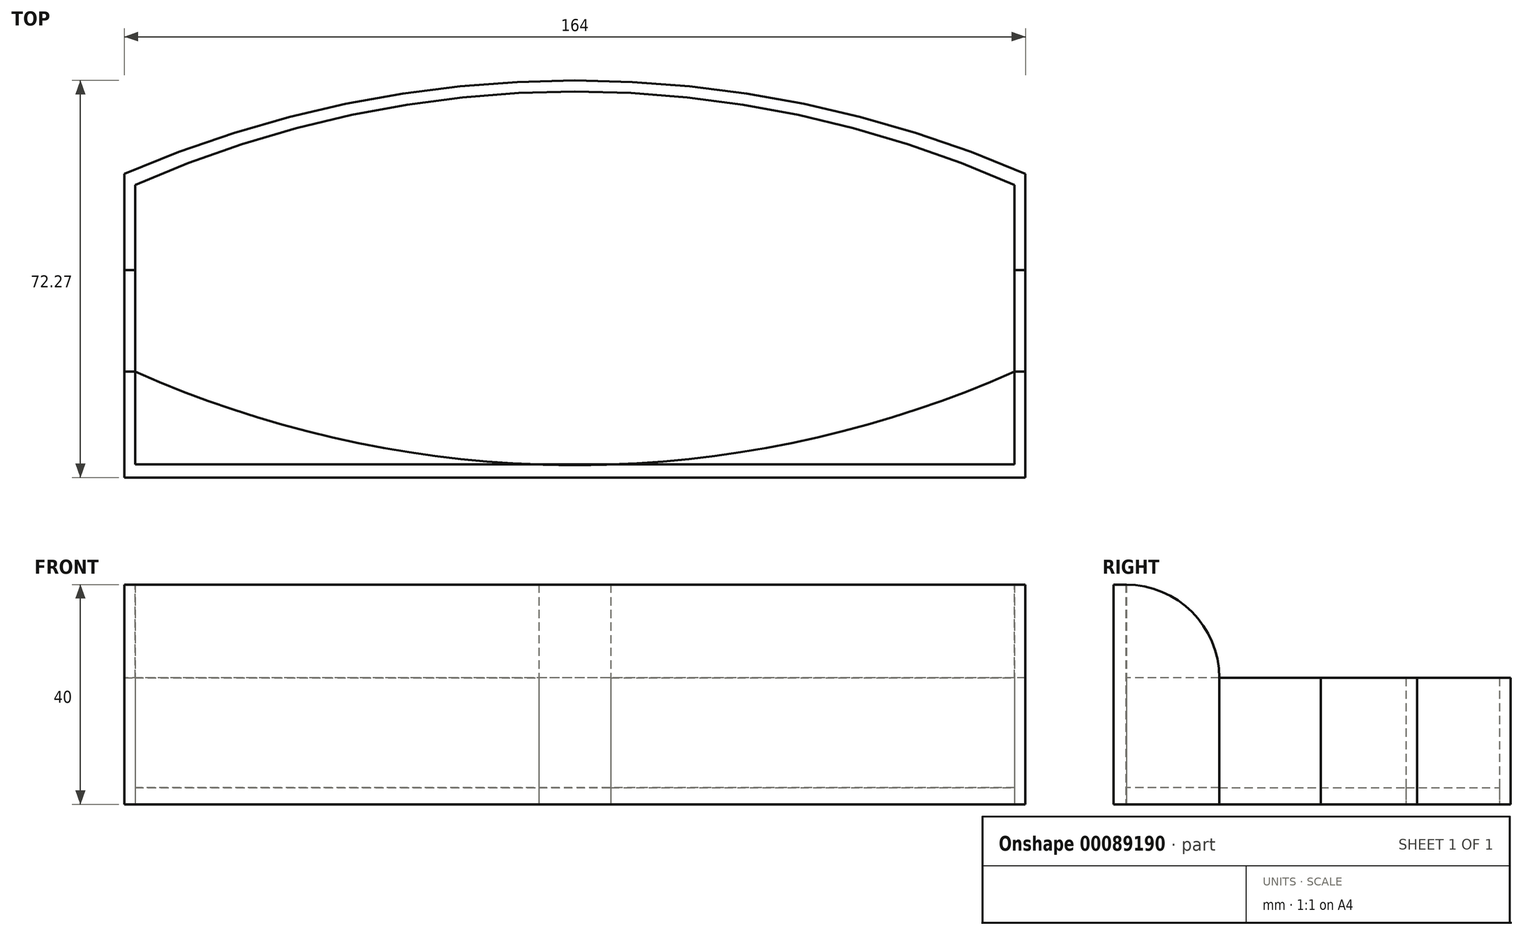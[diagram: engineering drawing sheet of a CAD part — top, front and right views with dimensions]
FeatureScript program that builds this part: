
annotation { "Feature Type Name" : "Feature", "Feature Type Description" : "" }
export const myFeature = defineFeature(function(context is Context, id is Id, definition is map)
    precondition{}
    {
        {
            var Q0;
            Q0=qCreatedBy(makeId("Top.planeOp"),FACE);
            var sketch = newSketch(context, id + "F0", { "sketchPlane" : qUnion([Q0])});
            skLineSegment(sketch, "E0.left", {"start": v(-58, 0) * mm, "end": v(-58, 15.5) * mm});
            skLineSegment(sketch, "E0.right", {"start": v(102, 0) * mm, "end": v(102, 15.5) * mm});
            skArc(sketch, "E1", {"start": v(102, 15.5) * mm, "mid": v(22, 32.5) * mm, "end": v(-58, 15.5) * mm});
            skLineSegment(sketch, "E2.left", {"start": v(-60, 0) * mm, "end": v(-60, 17.5) * mm});
            skLineSegment(sketch, "E2.right", {"start": v(104, 0) * mm, "end": v(104, 17.5) * mm});
            skArc(sketch, "E3", {"start": v(104, 17.5) * mm, "mid": v(22, 34.5) * mm, "end": v(-60, 17.5) * mm});
            skLineSegment(sketch, "E4.MirrorCS", {"start": v(-58, -3) * mm, "end": v(-58, -18.5) * mm});
            skLineSegment(sketch, "E5.MirrorCS", {"start": v(104, -3) * mm, "end": v(104, -20.5) * mm});
            skLineSegment(sketch, "E6.MirrorCS", {"start": v(-60, -3) * mm, "end": v(-60, -20.5) * mm});
            skLineSegment(sketch, "E7.MirrorCS", {"start": v(102, -3) * mm, "end": v(102, -18.5) * mm});
            skArc(sketch, "E8.MirrorCS", {"start": v(102, -18.5) * mm, "mid": v(22, -35.5) * mm, "end": v(-58, -18.5) * mm});
            skLineSegment(sketch, "E9.top", {"start": v(-60, -37.77) * mm, "end": v(104, -37.77) * mm});
            skLineSegment(sketch, "E9.left", {"start": v(-60, -20.5) * mm, "end": v(-60, -37.77) * mm});
            skLineSegment(sketch, "E9.right", {"start": v(104, -17.5) * mm, "end": v(104, -37.77) * mm});
            skLineSegment(sketch, "E10.top", {"start": v(-58, -35.4) * mm, "end": v(102, -35.4) * mm});
            skLineSegment(sketch, "E10.left", {"start": v(-58, -18.5) * mm, "end": v(-58, -35.4) * mm});
            skLineSegment(sketch, "E10.right", {"start": v(102, -15.5) * mm, "end": v(102, -35.4) * mm});
            skLineSegment(sketch, "E11", {"start": v(-58, -18.5) * mm, "end": v(-60, -18.5) * mm});
            skLineSegment(sketch, "E12", {"start": v(102, -18.5) * mm, "end": v(104, -18.5) * mm});
            skLineSegment(sketch, "E13", {"start": v(104, 0) * mm, "end": v(102, 0) * mm});
            skLineSegment(sketch, "E14", {"start": v(-60, 0) * mm, "end": v(-58, 0) * mm});
            skLineSegment(sketch, "E15", {"start": v(102, -3) * mm, "end": v(102, 0) * mm});
            skLineSegment(sketch, "E16", {"start": v(104, -3) * mm, "end": v(104, 0) * mm});
            skLineSegment(sketch, "E17", {"start": v(-58, -3) * mm, "end": v(-58, 0) * mm});
            skLineSegment(sketch, "E18", {"start": v(-60, -3) * mm, "end": v(-60, 0) * mm});
            skSolve(sketch);
        }
        {
            var Q0;
            Q0=makeQuery(id+"F0.imprint","IMPRINT",FACE,{"disambiguationData":[TD([[makeQuery(id+"F0.imprint","IMPRINT",EDGE,{"derivedFrom":sQuery(id+"F0.wireOp",EDGE,"E0.left")}),-1.0]])]});
            extrude(context, id + "F1", {"entities" : qUnion([Q0]), "depth" : 3 * mm});
        }
        {
            var Q0;
            Q0=makeQuery(id+"F0.imprint","IMPRINT",FACE,{"disambiguationData":[TD([[makeQuery(id+"F0.imprint","IMPRINT",EDGE,{"derivedFrom":sQuery(id+"F0.wireOp",EDGE,"E9.top")}),1.0]])]});
            extrude(context, id + "F2", {"entities" : qUnion([Q0]), "operationType" : NewBodyOperationType.ADD, "depth" : 40 * mm});
        }
        {
            var Q0;
            Q0=makeQuery(id+"F0.imprint","IMPRINT",FACE,{"disambiguationData":[TD([[makeQuery(id+"F0.imprint","IMPRINT",EDGE,{"derivedFrom":sQuery(id+"F0.wireOp",EDGE,"E0.left")}),1.0]])]});
            extrude(context, id + "F3", {"entities" : qUnion([Q0]), "depth" : 23 * mm});
        }
        {
            var Q0;
            {var subQ0=sQuery(id+"F0.wireOp",EDGE,"E10.right");Q0=makeQuery(id+"F0.imprint","IMPRINT",FACE,{"disambiguationData":[TD([[makeQuery(id+"F0.imprint","IMPRINT",EDGE,{"derivedFrom":subQ0}),-1.0]])]});}
            var Q1;
            {var subQ0=sQuery(id+"F0.wireOp",EDGE,"E10.left");Q1=makeQuery(id+"F0.imprint","IMPRINT",FACE,{"disambiguationData":[TD([[makeQuery(id+"F0.imprint","IMPRINT",EDGE,{"derivedFrom":subQ0}),1.0]])]});}
            extrude(context, id + "F4", {"entities" : qUnion([Q0, Q1]), "depth" : 23 * mm});
        }
        {
            var Q0;
            Q0=makeQuery(id+"F2.opExtrude","CAP_EDGE",EDGE,{"disambiguationData":[OSD([sQuery(id+"F0.wireOp",EDGE,"E11")])],"isStart":false});
            fillet(context, id + "F5", {"entities" : qUnion([Q0]), "radius" : 17 * mm, "tangentPropagation" : true, "allowEdgeOverflow" : false});
        }
        {
            var Q0;
            Q0=makeQuery(id+"F2.opExtrude","CAP_EDGE",EDGE,{"disambiguationData":[OSD([sQuery(id+"F0.wireOp",EDGE,"E12")])],"isStart":false});
            fillet(context, id + "F6", {"entities" : qUnion([Q0]), "radius" : 17 * mm, "tangentPropagation" : true, "allowEdgeOverflow" : false});
        }
        {
            var Q0;
            Q0=makeQuery(id+"F0.imprint","IMPRINT",FACE,{"disambiguationData":[TD([[makeQuery(id+"F0.imprint","IMPRINT",EDGE,{"derivedFrom":sQuery(id+"F0.wireOp",EDGE,"E4.MirrorCS")}),-1.0]])]});
            extrude(context, id + "F7", {"entities" : qUnion([Q0]), "depth" : 23 * mm});
        }
        {
            var Q0;
            {var subQ1=sQuery(id+"F0.wireOp",EDGE,"E5.MirrorCS");Q0=makeQuery(id+"F0.imprint","IMPRINT",FACE,{"disambiguationData":[TD([[makeQuery(id+"F0.imprint","IMPRINT",EDGE,{"derivedFrom":subQ1}),-1.0]])]});}
            extrude(context, id + "F8", {"entities" : qUnion([Q0]), "depth" : 23 * mm});
        }
    });
